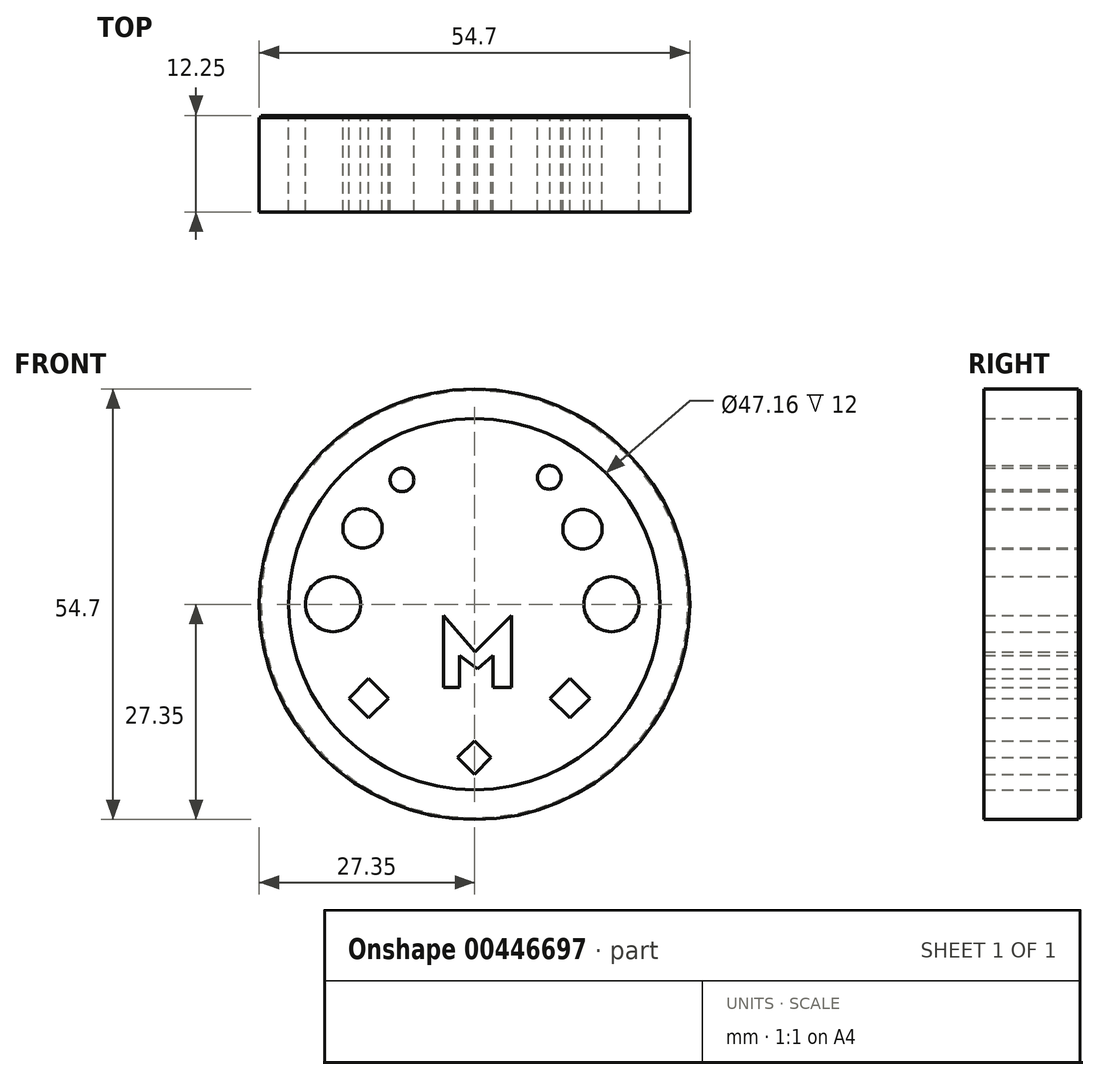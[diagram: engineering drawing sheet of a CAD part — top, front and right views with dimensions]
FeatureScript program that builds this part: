
annotation { "Feature Type Name" : "Feature", "Feature Type Description" : "" }
export const myFeature = defineFeature(function(context is Context, id is Id, definition is map)
    precondition{}
    {
        {
            var Q0;
            Q0=qCreatedBy(makeId("Front.planeOp"),FACE);
            var sketch = newSketch(context, id + "F0", { "sketchPlane" : qUnion([Q0])});
            skLineSegment(sketch, "E0", {"start": v(0.08, 11.46) * mm, "end": v(-3.9, 3.27) * mm});
            skLineSegment(sketch, "E1", {"start": v(-3.9, 3.27) * mm, "end": v(0.08, 11.46) * mm});
            skLineSegment(sketch, "E2", {"start": v(4.14, 3.27) * mm, "end": v(0.08, 11.46) * mm});
            skLineSegment(sketch, "E3", {"start": v(-3.9, 3.27) * mm, "end": v(-1.91, 3.27) * mm});
            skPoint(sketch, "E3.endSnap0", {"position": v(-1.91, 7.37) * mm});
            skLineSegment(sketch, "E4", {"start": v(4.14, 3.27) * mm, "end": v(2.1, 3.27) * mm});
            skPoint(sketch, "E4.endSnap0", {"position": v(2.1, 7.37) * mm});
            skLineSegment(sketch, "E5", {"start": v(2.1, 3.27) * mm, "end": v(0.08, 7.37) * mm});
            skLineSegment(sketch, "E6", {"start": v(0.08, 7.37) * mm, "end": v(-1.91, 3.27) * mm});
            skLineSegment(sketch, "E7", {"start": v(0.08, 9.43) * mm, "end": v(-0.48, 8.29) * mm});
            skLineSegment(sketch, "E8", {"start": v(-0.48, 8.29) * mm, "end": v(0.63, 8.29) * mm});
            skLineSegment(sketch, "E9", {"start": v(0.63, 8.29) * mm, "end": v(0.08, 9.43) * mm});
            skLineSegment(sketch, "E10", {"start": v(-3.9, -1.45) * mm, "end": v(-3.9, -10.6) * mm});
            skLineSegment(sketch, "E11", {"start": v(-3.9, -1.45) * mm, "end": v(0.08, -6.07) * mm});
            skLineSegment(sketch, "E12", {"start": v(0.08, -6.07) * mm, "end": v(4.7, -1.45) * mm});
            skLineSegment(sketch, "E13", {"start": v(4.7, -1.45) * mm, "end": v(4.7, -10.6) * mm});
            skLineSegment(sketch, "E14", {"start": v(-3.9, -10.6) * mm, "end": v(-1.91, -10.6) * mm});
            skPoint(sketch, "E14.endSnap0", {"position": v(-1.91, -3.76) * mm});
            skLineSegment(sketch, "E15", {"start": v(4.7, -10.6) * mm, "end": v(2.39, -10.6) * mm});
            skPoint(sketch, "E15.endSnap0", {"position": v(2.39, -3.76) * mm});
            skLineSegment(sketch, "E16", {"start": v(2.39, -10.6) * mm, "end": v(2.39, -6.5) * mm});
            skLineSegment(sketch, "E17", {"start": v(2.39, -6.5) * mm, "end": v(0.4, -8.2) * mm});
            skLineSegment(sketch, "E18", {"start": v(-1.91, -10.6) * mm, "end": v(-1.91, -6.5) * mm});
            skLineSegment(sketch, "E19", {"start": v(-1.91, -6.5) * mm, "end": v(0.4, -8.2) * mm});
            skCircle(sketch, "E20", {"center": v(0, 0) * mm, "radius": 27.5 * mm});
            skCircle(sketch, "E21", {"center": v(0, 0) * mm, "radius": 23.58 * mm});
            skCircle(sketch, "E22", {"center": v(17.4, 0) * mm, "radius": 3.5 * mm});
            skCircle(sketch, "E23", {"center": v(-17.97, 0) * mm, "radius": 3.5 * mm});
            skCircle(sketch, "E24", {"center": v(-14.22, 9.63) * mm, "radius": 2.5 * mm});
            skCircle(sketch, "E25", {"center": v(-9.2, 15.8) * mm, "radius": 1.5 * mm});
            skCircle(sketch, "E26", {"center": v(9.5, 16.1) * mm, "radius": 1.5 * mm});
            skCircle(sketch, "E27", {"center": v(13.72, 9.53) * mm, "radius": 2.5 * mm});
            skLineSegment(sketch, "E28", {"start": v(0, -17.35) * mm, "end": v(-2.12, -19.47) * mm});
            skLineSegment(sketch, "E29", {"start": v(-2.12, -19.47) * mm, "end": v(0, -21.6) * mm});
            skLineSegment(sketch, "E30", {"start": v(0, -21.6) * mm, "end": v(2.12, -19.47) * mm});
            skLineSegment(sketch, "E31", {"start": v(2.12, -19.47) * mm, "end": v(0, -17.35) * mm});
            skLineSegment(sketch, "E32", {"start": v(-13.43, -9.43) * mm, "end": v(-15.95, -11.95) * mm});
            skLineSegment(sketch, "E33", {"start": v(-15.95, -11.95) * mm, "end": v(-13.43, -14.46) * mm});
            skLineSegment(sketch, "E34", {"start": v(-13.43, -14.46) * mm, "end": v(-10.92, -11.95) * mm});
            skLineSegment(sketch, "E35", {"start": v(-10.92, -11.95) * mm, "end": v(-13.43, -9.43) * mm});
            skLineSegment(sketch, "E36", {"start": v(9.62, -11.95) * mm, "end": v(12.13, -9.43) * mm});
            skLineSegment(sketch, "E37", {"start": v(12.13, -9.43) * mm, "end": v(14.64, -11.95) * mm});
            skLineSegment(sketch, "E38", {"start": v(14.64, -11.95) * mm, "end": v(12.13, -14.46) * mm});
            skLineSegment(sketch, "E39", {"start": v(12.13, -14.46) * mm, "end": v(9.62, -11.95) * mm});
            skCircle(sketch, "E40", {"center": v(0, 0) * mm, "radius": 27.35 * mm});
            skSolve(sketch);
        }
        {
            var Q0;
            Q0=makeQuery(id+"F0.imprint","IMPRINT",FACE,{"disambiguationData":[TD([[makeQuery(id+"F0.imprint","IMPRINT",EDGE,{"derivedFrom":sQuery(id+"F0.wireOp",EDGE,"E22")}),1.0]])]});
            var Q1;
            Q1=makeQuery(id+"F0.imprint","IMPRINT",FACE,{"disambiguationData":[TD([[makeQuery(id+"F0.imprint","IMPRINT",EDGE,{"derivedFrom":sQuery(id+"F0.wireOp",EDGE,"E26")}),1.0]])]});
            var Q2;
            Q2=makeQuery(id+"F0.imprint","IMPRINT",FACE,{"disambiguationData":[TD([[makeQuery(id+"F0.imprint","IMPRINT",EDGE,{"derivedFrom":sQuery(id+"F0.wireOp",EDGE,"E25")}),1.0]])]});
            var Q3;
            Q3=makeQuery(id+"F0.imprint","IMPRINT",FACE,{"disambiguationData":[TD([[makeQuery(id+"F0.imprint","IMPRINT",EDGE,{"derivedFrom":sQuery(id+"F0.wireOp",EDGE,"E24")}),1.0]])]});
            var Q4;
            Q4=makeQuery(id+"F0.imprint","IMPRINT",FACE,{"disambiguationData":[TD([[makeQuery(id+"F0.imprint","IMPRINT",EDGE,{"derivedFrom":sQuery(id+"F0.wireOp",EDGE,"E27")}),1.0]])]});
            var Q5;
            Q5=makeQuery(id+"F0.imprint","IMPRINT",FACE,{"disambiguationData":[TD([[makeQuery(id+"F0.imprint","IMPRINT",EDGE,{"derivedFrom":sQuery(id+"F0.wireOp",EDGE,"E21")}),-1.0]])]});
            var Q6;
            Q6=makeQuery(id+"F0.imprint","IMPRINT",FACE,{"disambiguationData":[TD([[makeQuery(id+"F0.imprint","IMPRINT",EDGE,{"derivedFrom":sQuery(id+"F0.wireOp",EDGE,"E23")}),1.0]])]});
            var Q7;
            Q7=makeQuery(id+"F0.imprint","IMPRINT",FACE,{"disambiguationData":[TD([[makeQuery(id+"F0.imprint","IMPRINT",EDGE,{"derivedFrom":sQuery(id+"F0.wireOp",EDGE,"E10")}),1.0]])]});
            var Q8;
            Q8=makeQuery(id+"F0.imprint","IMPRINT",FACE,{"disambiguationData":[TD([[makeQuery(id+"F0.imprint","IMPRINT",EDGE,{"derivedFrom":sQuery(id+"F0.wireOp",EDGE,"E36")}),-1.0]])]});
            var Q9;
            Q9=makeQuery(id+"F0.imprint","IMPRINT",FACE,{"disambiguationData":[TD([[makeQuery(id+"F0.imprint","IMPRINT",EDGE,{"derivedFrom":sQuery(id+"F0.wireOp",EDGE,"E28")}),1.0]])]});
            var Q10;
            Q10=makeQuery(id+"F0.imprint","IMPRINT",FACE,{"disambiguationData":[TD([[makeQuery(id+"F0.imprint","IMPRINT",EDGE,{"derivedFrom":sQuery(id+"F0.wireOp",EDGE,"E32")}),1.0]])]});
            var Q11;
            Q11=makeQuery(id+"F0.imprint","IMPRINT",FACE,{"disambiguationData":[TD([[makeQuery(id+"F0.imprint","IMPRINT",EDGE,{"derivedFrom":sQuery(id+"F0.wireOp",EDGE,"E1")}),-1.0]])]});
            extrude(context, id + "F1", {"entities" : qUnion([Q0, Q1, Q2, Q3, Q4, Q5, Q6, Q7, Q8, Q9, Q10, Q11]), "depth" : 12 * mm});
        }
        {
            var Q0;
            Q0=qCreatedBy(makeId("Front.planeOp"),FACE);
            var sketch = newSketch(context, id + "F2", { "sketchPlane" : qUnion([Q0])});
            skCircle(sketch, "E41", {"center": v(0, 0) * mm, "radius": 27.13 * mm});
            skSolve(sketch);
        }
        {
            var Q0;
            Q0 = qSketchRegion(id + "F2", true);
            extrude(context, id + "F3", {"entities" : qUnion([Q0]), "oppositeDirection" : true, "depth" : 0.25 * mm});
        }
    });
